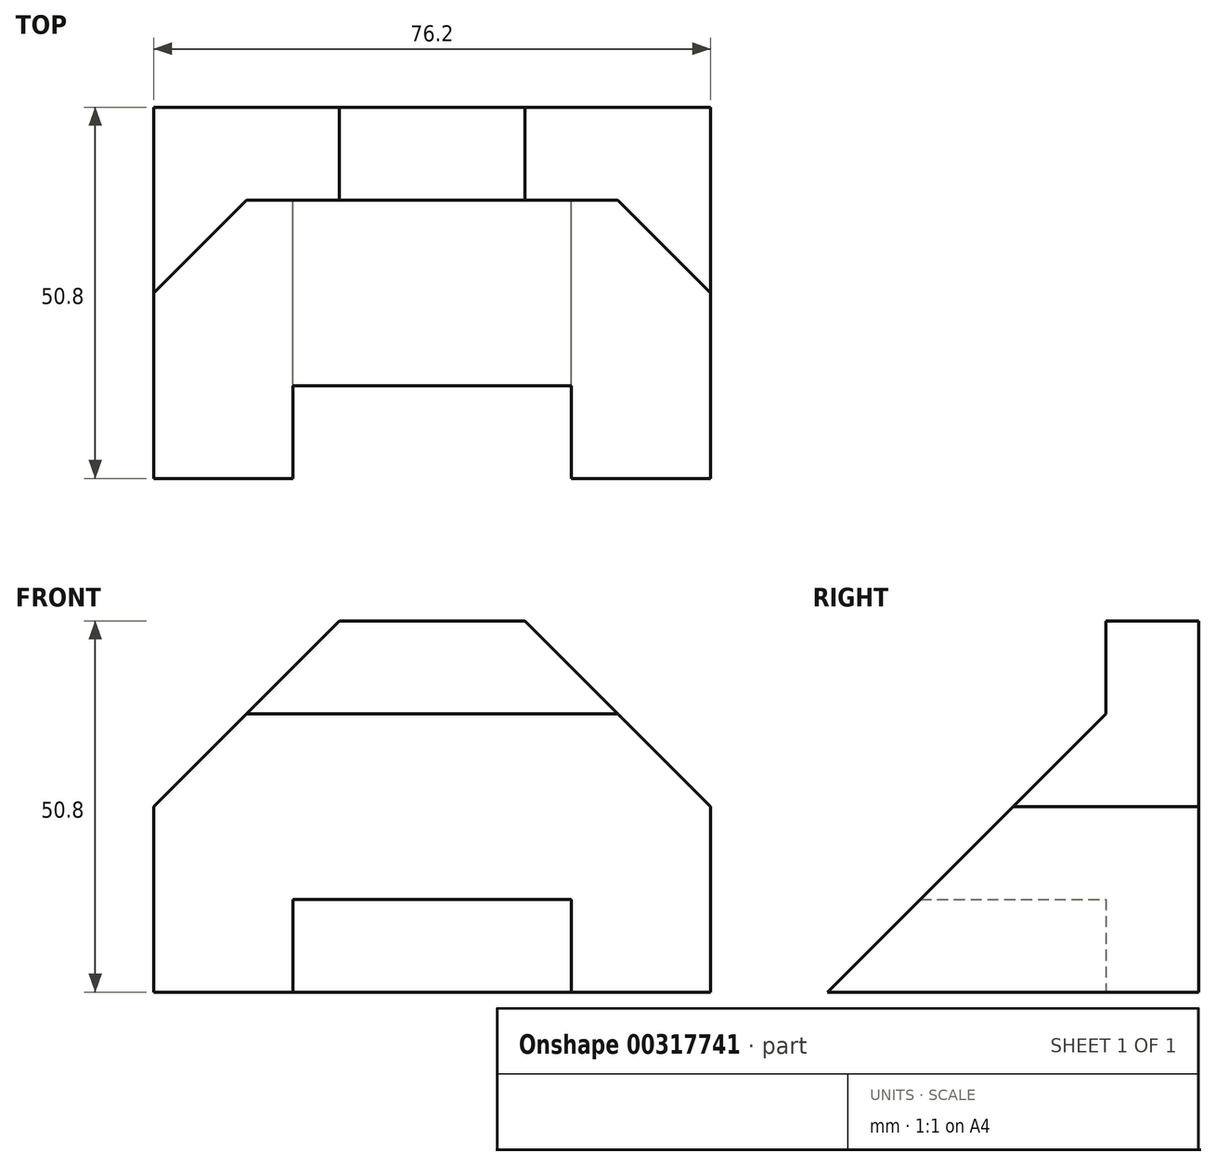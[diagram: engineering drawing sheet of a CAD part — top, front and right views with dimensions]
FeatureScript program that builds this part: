
annotation { "Feature Type Name" : "Feature", "Feature Type Description" : "" }
export const myFeature = defineFeature(function(context is Context, id is Id, definition is map)
    precondition{}
    {
        {
            var Q0;
            Q0=qCreatedBy(makeId("Front.planeOp"),FACE);
            var sketch = newSketch(context, id + "F0", { "sketchPlane" : qUnion([Q0])});
            skLineSegment(sketch, "E0.bottom", {"start": v(0, 0) * mm, "end": v(76.2, 0) * mm});
            skLineSegment(sketch, "E0.left", {"start": v(0, 0) * mm, "end": v(0, 25.4) * mm});
            skLineSegment(sketch, "E0.right", {"start": v(76.2, 0) * mm, "end": v(76.2, 25.4) * mm});
            skLineSegment(sketch, "E1.bottom", {"start": v(50.8, 50.8) * mm, "end": v(25.4, 50.8) * mm});
            skLineSegment(sketch, "E2", {"start": v(50.8, 50.8) * mm, "end": v(76.2, 25.4) * mm});
            skLineSegment(sketch, "E3", {"start": v(25.4, 50.8) * mm, "end": v(0, 25.4) * mm});
            skPoint(sketch, "E4", {"position": v(38.1, 38.1) * mm});
            skPoint(sketch, "E4.positionSnap0", {"position": v(38.1, 50.8) * mm});
            skLineSegment(sketch, "E5", {"start": v(38.1, 38.1) * mm, "end": v(0, 0) * mm});
            skLineSegment(sketch, "E6", {"start": v(38.1, 38.1) * mm, "end": v(76.2, 0) * mm});
            skLineSegment(sketch, "E7.bottom", {"start": v(57.15, 12.7) * mm, "end": v(19.05, 12.7) * mm});
            skLineSegment(sketch, "E7.left", {"start": v(57.15, 12.7) * mm, "end": v(57.15, 0) * mm});
            skLineSegment(sketch, "E7.right", {"start": v(19.05, 12.7) * mm, "end": v(19.05, 0) * mm});
            skPoint(sketch, "E7.middle", {"position": v(38.1, 0) * mm});
            skLineSegment(sketch, "E8", {"start": v(0, 25.4) * mm, "end": v(0, 50.8) * mm});
            skLineSegment(sketch, "E9", {"start": v(0, 50.8) * mm, "end": v(25.4, 50.8) * mm});
            skLineSegment(sketch, "E10", {"start": v(50.8, 50.8) * mm, "end": v(76.2, 50.8) * mm});
            skLineSegment(sketch, "E11", {"start": v(76.2, 50.8) * mm, "end": v(76.2, 25.4) * mm});
            skSolve(sketch);
        }
        {
            var Q0;
            Q0=makeQuery(id+"F0.imprint","IMPRINT",FACE,{"disambiguationData":[TD([[makeQuery(id+"F0.imprint","IMPRINT",EDGE,{"derivedFrom":sQuery(id+"F0.wireOp",EDGE,"E0.left")}),-1.0]])]});
            var Q1;
            {var subQ1=sQuery(id+"F0.wireOp",EDGE,"E5");Q1=makeQuery(id+"F0.imprint","IMPRINT",FACE,{"disambiguationData":[TD([[makeQuery(id+"F0.imprint","IMPRINT",EDGE,{"derivedFrom":subQ1}),1.0]])]});}
            var Q2;
            Q2=makeQuery(id+"F0.imprint","IMPRINT",FACE,{"disambiguationData":[TD([[makeQuery(id+"F0.imprint","IMPRINT",EDGE,{"derivedFrom":sQuery(id+"F0.wireOp",EDGE,"E7.bottom")}),1.0]])]});
            extrude(context, id + "F1", {"entities" : qUnion([Q0, Q1, Q2]), "oppositeDirection" : true, "depth" : 12.7 * mm});
        }
        {
            var Q0;
            Q0=qCreatedBy(makeId("Right.planeOp"),FACE);
            var sketch = newSketch(context, id + "F2", { "sketchPlane" : qUnion([Q0])});
            skLineSegment(sketch, "E12", {"start": v(0, 0) * mm, "end": v(0, 38.1) * mm});
            skLineSegment(sketch, "E13", {"start": v(0, 0) * mm, "end": v(-38.1, 0) * mm});
            skLineSegment(sketch, "E14", {"start": v(-38.1, 0) * mm, "end": v(0, 38.1) * mm});
            skSolve(sketch);
        }
        {
            var Q0;
            Q0 = qSketchRegion(id + "F2", true);
            extrude(context, id + "F3", {"entities" : qUnion([Q0]), "operationType" : NewBodyOperationType.ADD, "depth" : 76.2 * mm});
        }
        {
            var Q0;
            {var subQ1=sQuery(id+"F2.wireOp",EDGE,"E12");var subQ3=sQuery(id+"F0.wireOp",EDGE,"E0.left");Q0=makeQuery(id+"F3.boolean.opBoolean","SPLIT",FACE,{"disambiguationData":[TD([makeQuery(id+"F1.opExtrude","SWEPT_FACE",FACE,{"disambiguationData":[OSD([subQ3])]})])],"derivedFrom":makeQuery(id+"F3.opExtrude","SWEPT_FACE",FACE,{"disambiguationData":[OSD([subQ1])]})});}
            var Q1;
            {var subQ1=sQuery(id+"F2.wireOp",EDGE,"E12");var subQ2=sQuery(id+"F0.wireOp",EDGE,"E0.right");Q1=makeQuery(id+"F3.boolean.opBoolean","SPLIT",FACE,{"disambiguationData":[TD([makeQuery(id+"F1.opExtrude","SWEPT_FACE",FACE,{"disambiguationData":[OSD([subQ2])]})])],"derivedFrom":makeQuery(id+"F3.opExtrude","SWEPT_FACE",FACE,{"disambiguationData":[OSD([subQ1])]})});}
            extrude(context, id + "F4", {"entities" : qUnion([Q0, Q1]), "operationType" : NewBodyOperationType.REMOVE, "endBound" : BoundingType.THROUGH_ALL, "oppositeDirection" : true, "depth" : 25.4 * mm});
        }
        {
            var Q0;
            Q0=makeQuery(id+"F0.imprint","IMPRINT",FACE,{"disambiguationData":[TD([[makeQuery(id+"F0.imprint","IMPRINT",EDGE,{"derivedFrom":sQuery(id+"F0.wireOp",EDGE,"E7.bottom")}),1.0]])]});
            extrude(context, id + "F5", {"entities" : qUnion([Q0]), "operationType" : NewBodyOperationType.REMOVE, "endBound" : BoundingType.THROUGH_ALL, "depth" : 25.4 * mm});
        }
    });
